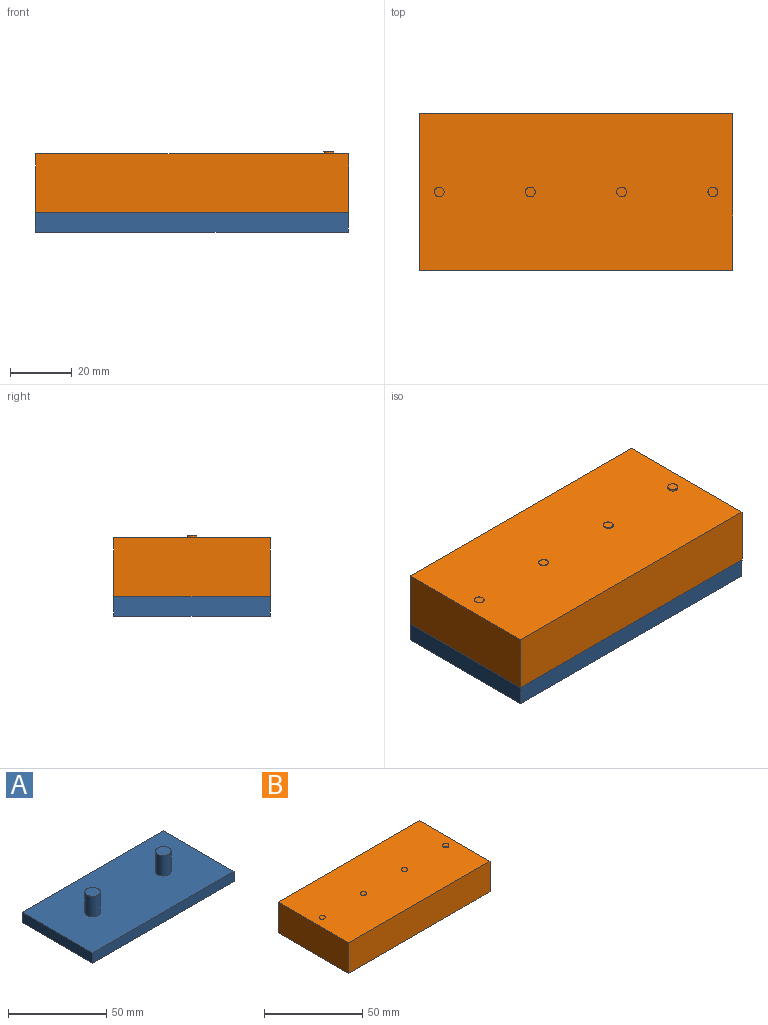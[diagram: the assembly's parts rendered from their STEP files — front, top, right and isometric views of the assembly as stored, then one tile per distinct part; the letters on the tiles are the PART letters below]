
ASSEMBLY  parts=2 mates=1
PART A: 10 faces, bbox 101.6x50.8x19.1 mm
  f0: plane 101.6x6.35mm, normal (0,-1,0), area 645.2mm2, adj f1,f3,f4,f5
  f1: plane 50.8x6.35mm, normal (1,0,0), area 322.6mm2, adj f0,f2,f4,f5
  f2: plane 101.6x6.35mm, normal (0,1,0), area 645.2mm2, adj f1,f3,f4,f5
  f3: plane 50.8x6.35mm, normal (-1,0,0), area 322.6mm2, adj f0,f2,f4,f5
  f4: plane 101.6x50.8mm, normal (0,0,1), area 5062.3mm2, adj f0,f1,f2,f3,f6,f8
  f5: plane 101.6x50.8mm, normal (0,0,-1), area 5161.3mm2, adj f0,f1,f2,f3
  f6: cylinder r=3.97mm len=12.7mm, axis (0,0,-1), area 316.7mm2, adj f4,f7
  f7: plane 7.94x7.94mm, normal (0,0,1), area 49.5mm2, adj f6
  f8: cylinder r=3.97mm len=12.7mm, axis (0,0,-1), area 316.7mm2, adj f4,f9
  f9: plane 7.94x7.94mm, normal (0,0,1), area 49.5mm2, adj f8
PART B: 18 faces, bbox 101.6x50.8x19.7 mm
  f0: plane 101.6x19.05mm, normal (0,-1,0), area 1935.5mm2, adj f1,f3,f4,f5
  f1: plane 50.8x19.05mm, normal (1,0,0), area 967.7mm2, adj f0,f2,f4,f5
  f2: plane 101.6x19.05mm, normal (0,1,0), area 1935.5mm2, adj f1,f3,f4,f5
  f3: plane 50.8x19.05mm, normal (-1,0,0), area 967.7mm2, adj f0,f2,f4,f5
  f4: plane 101.6x50.8mm, normal (0,0,1), area 5129.6mm2, adj f0,f1,f2,f3,f6,f8,f10,f12
  f5: plane 101.6x50.8mm, normal (0,0,-1), area 5062.3mm2, adj f0,f1,f2,f3,f14,f16
  f6: cylinder r=1.59mm len=3.18mm, axis (0,0,-1), area 0.5mm2, adj f4,f7
  f7: plane 3.18x3.18mm, normal (0,0,1), area 7.9mm2, adj f6
  f8: cylinder r=1.59mm len=3.18mm, axis (0,0,-1), area 1.3mm2, adj f4,f9
  f9: plane 3.18x3.18mm, normal (0,0,1), area 7.9mm2, adj f8
  f10: cylinder r=1.59mm len=3.18mm, axis (0,0,-1), area 2.5mm2, adj f4,f11
  f11: plane 3.18x3.18mm, normal (0,0,1), area 7.9mm2, adj f10
  f12: cylinder r=1.59mm len=3.18mm, axis (0,0,-1), area 6.3mm2, adj f4,f13
  f13: plane 3.18x3.18mm, normal (0,0,1), area 7.9mm2, adj f12
  f14: cylinder r=3.97mm len=12.7mm, axis (0,0,-1), area 316.7mm2, adj f5,f15
  f15: plane 7.94x7.94mm, normal (0,0,-1), area 49.5mm2, adj f14
  f16: cylinder r=3.97mm len=12.7mm, axis (0,0,-1), area 316.7mm2, adj f5,f17
  f17: plane 7.94x7.94mm, normal (0,0,-1), area 49.5mm2, adj f16
PLACE A t=(-26.93,8.38,-15.26)mm
PLACE B t=(-22.32,8.38,-8.91)mm
MATE fastened A.f4 <-> B.f5  axis (0,0,1) through (-26.93,8.38,-8.91)mm
